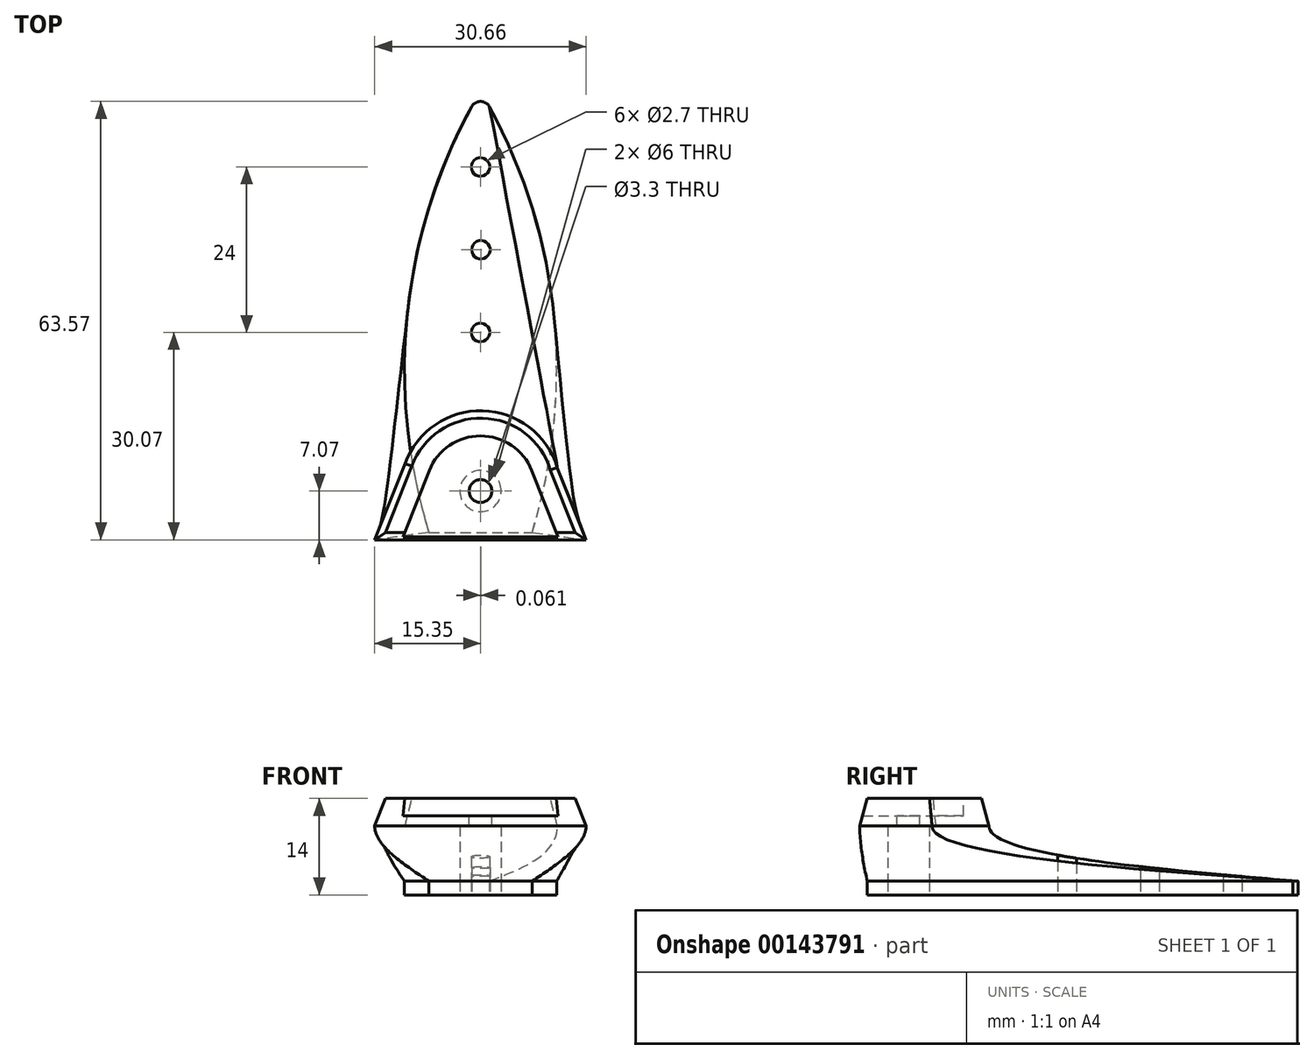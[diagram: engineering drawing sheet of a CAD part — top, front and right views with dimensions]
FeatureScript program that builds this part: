
annotation { "Feature Type Name" : "Feature", "Feature Type Description" : "" }
export const myFeature = defineFeature(function(context is Context, id is Id, definition is map)
    precondition{}
    {
        {
            var Q0;
            Q0=qCreatedBy(makeId("Top.planeOp"),FACE);
            var sketch = newSketch(context, id + "F0", { "sketchPlane" : qUnion([Q0])});
            skLineSegment(sketch, "E0", {"start": v(9.68, 4.17) * mm, "end": v(13.73, -6) * mm});
            skLineSegment(sketch, "E1", {"start": v(-9.84, 3.86) * mm, "end": v(-13.77, -6) * mm});
            skArc(sketch, "E2.trimOffspring", {"start": v(10.13, 3.06) * mm, "mid": v(0.29, 10.57) * mm, "end": v(-9.94, 3.6) * mm});
            skLineSegment(sketch, "E3", {"start": v(-13.77, -6) * mm, "end": v(13.73, -6) * mm});
            skCircle(sketch, "E4", {"center": v(0, 0) * mm, "radius": 1.65 * mm});
            skSolve(sketch);
        }
        {
            var Q0;
            {var subQ1=sQuery(id+"F0.wireOp",EDGE,"E2.trimOffspring");Q0=makeQuery(id+"F0.imprint","IMPRINT",FACE,{"disambiguationData":[TD([[makeQuery(id+"F0.imprint","IMPRINT",EDGE,{"derivedFrom":subQ1}),1.0]])]});}
            var Q1;
            Q1=makeQuery(id+"F0.imprint","IMPRINT",FACE,{"disambiguationData":[TD([[makeQuery(id+"F0.imprint","IMPRINT",EDGE,{"derivedFrom":sQuery(id+"F0.wireOp",EDGE,"E4")}),1.0]])]});
            extrude(context, id + "F1", {"entities" : qUnion([Q0, Q1]), "oppositeDirection" : true, "depth" : 4 * mm, "hasDraft" : true, "draftAngle" : 15 * degree});
        }
        {
            var Q0;
            Q0=qCreatedBy(makeId("Top.planeOp"),FACE);
            var sketch = newSketch(context, id + "F2", { "sketchPlane" : qUnion([Q0])});
            skPoint(sketch, "E5.middle", {"position": v(0, 0) * mm});
            skArc(sketch, "E6", {"start": v(7.43, 2.96) * mm, "mid": v(0, 8) * mm, "end": v(-7.43, 2.96) * mm});
            skLineSegment(sketch, "E7", {"start": v(-11, -6) * mm, "end": v(-7.43, 2.96) * mm});
            skLineSegment(sketch, "E8", {"start": v(11, -6) * mm, "end": v(7.43, 2.96) * mm});
            skLineSegment(sketch, "E9", {"start": v(11, -6) * mm, "end": v(11.89, -8.23) * mm});
            skLineSegment(sketch, "E10", {"start": v(-11, -6) * mm, "end": v(-11.89, -8.23) * mm});
            skLineSegment(sketch, "E11", {"start": v(11.89, -8.23) * mm, "end": v(-11.89, -8.23) * mm});
            skSolve(sketch);
        }
        {
            var Q0;
            Q0=makeQuery(id+"F2.imprint","IMPRINT",FACE,{"disambiguationData":[TD([[makeQuery(id+"F2.imprint","IMPRINT",EDGE,{"derivedFrom":sQuery(id+"F2.wireOp",EDGE,"E6")}),1.0]])]});
            extrude(context, id + "F3", {"entities" : qUnion([Q0]), "operationType" : NewBodyOperationType.REMOVE, "oppositeDirection" : true, "depth" : 2.5 * mm});
        }
        {
            var Q0;
            Q0=makeQuery(id+"F1.opExtrude","CAP_FACE",FACE,{"disambiguationData":[OSD([sQuery(id+"F0.wireOp",EDGE,"E0"),sQuery(id+"F0.wireOp",EDGE,"E1"),sQuery(id+"F0.wireOp",EDGE,"E2.trimOffspring"),sQuery(id+"F0.wireOp",EDGE,"E3"),sQuery(id+"F0.wireOp",EDGE,"E4")])],"isStart":false});
            cPlane(context, id + "F4", {"entities" : qUnion([Q0]), "cplaneType" : CPlaneType.OFFSET, "offset" : 10 * mm, "width" : 150 * mm, "height" : 150 * mm});
        }
        {
            var Q0;
            Q0=qCreatedBy(id+"F4.planeOp",FACE);
            var sketch = newSketch(context, id + "F5", { "sketchPlane" : qUnion([Q0])});
            skArc(sketch, "E12", {"start": v(-1.3, -55.76) * mm, "mid": v(0, -56.5) * mm, "end": v(1.3, -55.76) * mm});
            skArc(sketch, "E13", {"start": v(-7.5, 6) * mm, "mid": v(-10.63, -25.5) * mm, "end": v(-1.3, -55.76) * mm});
            skArc(sketch, "E14.MirrorCS", {"start": v(7.5, 6) * mm, "mid": v(10.63, -25.5) * mm, "end": v(1.3, -55.76) * mm});
            skLineSegment(sketch, "E15", {"start": v(-7.5, 6) * mm, "end": v(7.5, 6) * mm});
            skSolve(sketch);
        }
        {
            var Q0;
            Q0=makeQuery(id+"F5.imprint","IMPRINT",FACE,{"disambiguationData":[TD([[makeQuery(id+"F5.imprint","IMPRINT",EDGE,{"derivedFrom":sQuery(id+"F5.wireOp",EDGE,"E12")}),1.0]])]});
            extrude(context, id + "F6", {"entities" : qUnion([Q0]), "oppositeDirection" : true, "depth" : 2 * mm});
        }
        {
            var Q0;
            Q0=makeQuery(id+"F6.opExtrude","CAP_FACE",FACE,{"disambiguationData":[OSD([sQuery(id+"F5.wireOp",EDGE,"E12"),sQuery(id+"F5.wireOp",EDGE,"E13"),sQuery(id+"F5.wireOp",EDGE,"E14.MirrorCS"),sQuery(id+"F5.wireOp",EDGE,"E15")])],"isStart":false});
            var Q1;
            Q1=makeQuery(id+"F1.opExtrude","CAP_FACE",FACE,{"disambiguationData":[OSD([sQuery(id+"F0.wireOp",EDGE,"E0"),sQuery(id+"F0.wireOp",EDGE,"E1"),sQuery(id+"F0.wireOp",EDGE,"E2.trimOffspring"),sQuery(id+"F0.wireOp",EDGE,"E3"),sQuery(id+"F0.wireOp",EDGE,"E4")])],"isStart":false});
            var Q2;
            Q2=makeQuery(id+"F1.opExtrude","CAP_FACE",FACE,{"disambiguationData":[OSD([sQuery(id+"F0.wireOp",EDGE,"E0"),sQuery(id+"F0.wireOp",EDGE,"E1"),sQuery(id+"F0.wireOp",EDGE,"E2.trimOffspring"),sQuery(id+"F0.wireOp",EDGE,"E3"),sQuery(id+"F0.wireOp",EDGE,"E4")])],"isStart":false});
            var Q3;
            Q3=makeQuery(id+"F6.opExtrude","CAP_FACE",FACE,{"disambiguationData":[OSD([sQuery(id+"F5.wireOp",EDGE,"E12"),sQuery(id+"F5.wireOp",EDGE,"E13"),sQuery(id+"F5.wireOp",EDGE,"E14.MirrorCS"),sQuery(id+"F5.wireOp",EDGE,"E15")])],"isStart":false});
            var Q4;
            Q4=makeQuery(id+"F1.opExtrude","CAP_VERTEX",VERTEX,{"disambiguationData":[OSD([sQuery(id+"F0.wireOp",EDGE,"E0"),sQuery(id+"F0.wireOp",EDGE,"E3")])],"isStart":false});
            var Q5;
            Q5=makeQuery(id+"F6.opExtrude","CAP_VERTEX",VERTEX,{"disambiguationData":[OSD([sQuery(id+"F5.wireOp",EDGE,"E14.MirrorCS"),sQuery(id+"F5.wireOp",EDGE,"E15")])],"isStart":false});
            loft(context, id + "F7", {"endCondition" : LoftEndDerivativeType.NORMAL_TO_PROFILE, "endMagnitude" : 1, "sheetProfilesArray" : [{ "sheetProfileEntities" : qUnion([Q0]) }, { "sheetProfileEntities" : qUnion([Q1]) }], "wireProfilesArray" : [{ "wireProfileEntities" : qUnion([Q2]) }, { "wireProfileEntities" : qUnion([Q3]) }], "connections" : [{ "connectionEntities" : qUnion([Q4, Q5]), "connectionEdgeQueries" : qUnion([]), "connectionEdgeParameters" : [] }]});
        }
        {
            var Q0;
            Q0=makeQuery(id+"F3.boolean.opBoolean","COPY",FACE,{"derivedFrom":makeQuery(id+"F3.opExtrude","CAP_FACE",FACE,{"disambiguationData":[OSD([sQuery(id+"F2.wireOp",EDGE,"E6"),sQuery(id+"F2.wireOp",EDGE,"E7"),sQuery(id+"F2.wireOp",EDGE,"E8"),sQuery(id+"F2.wireOp",EDGE,"E9"),sQuery(id+"F2.wireOp",EDGE,"E10"),sQuery(id+"F2.wireOp",EDGE,"E11")])],"isStart":false})});
            var sketch = newSketch(context, id + "F8", { "sketchPlane" : qUnion([Q0])});
            skCircle(sketch, "E16", {"center": v(0, 0) * mm, "radius": 1.65 * mm});
            skSolve(sketch);
        }
        {
            var Q0;
            Q0 = qSketchRegion(id + "F8", true);
            extrude(context, id + "F9", {"entities" : qUnion([Q0]), "operationType" : NewBodyOperationType.REMOVE, "oppositeDirection" : true, "depth" : 25 * mm});
        }
        {
            var Q0;
            Q0=makeQuery(id+"F6.opExtrude","CAP_FACE",FACE,{"disambiguationData":[OSD([sQuery(id+"F5.wireOp",EDGE,"E12"),sQuery(id+"F5.wireOp",EDGE,"E13"),sQuery(id+"F5.wireOp",EDGE,"E14.MirrorCS"),sQuery(id+"F5.wireOp",EDGE,"E15")])],"isStart":true});
            var sketch = newSketch(context, id + "F10", { "sketchPlane" : qUnion([Q0])});
            skCircle(sketch, "E17", {"center": v(0, 0) * mm, "radius": 3 * mm});
            skCircle(sketch, "E18", {"center": v(0, -47) * mm, "radius": 1.35 * mm});
            skCircle(sketch, "E19", {"center": v(0.06, -35) * mm, "radius": 1.35 * mm});
            skCircle(sketch, "E20", {"center": v(0, -23) * mm, "radius": 1.35 * mm});
            skSolve(sketch);
        }
        {
            var Q0;
            Q0 = qSketchRegion(id + "F10", true);
            extrude(context, id + "F11", {"entities" : qUnion([Q0]), "operationType" : NewBodyOperationType.REMOVE, "oppositeDirection" : true, "depth" : 10 * mm});
        }
    });
